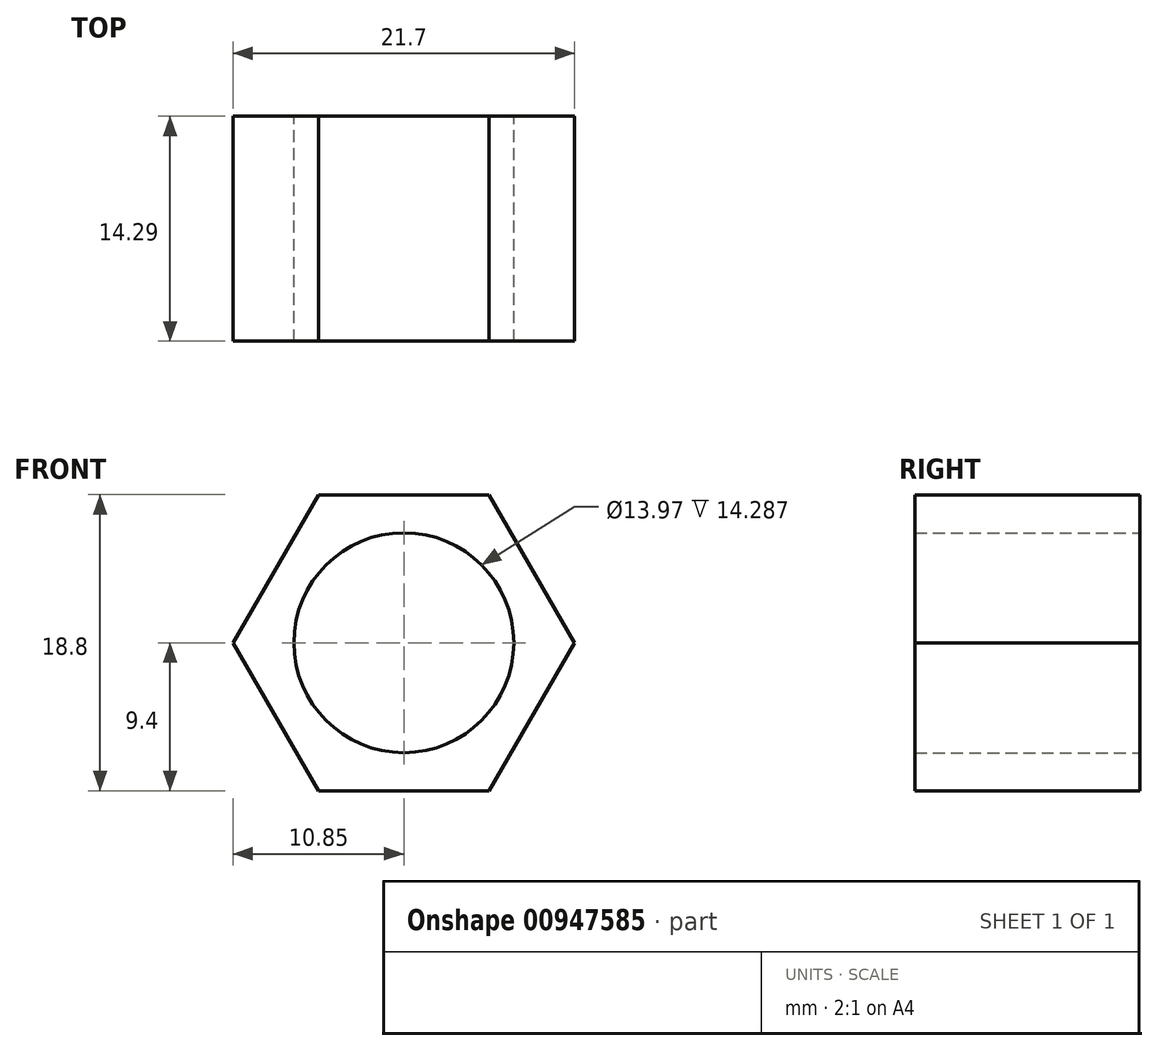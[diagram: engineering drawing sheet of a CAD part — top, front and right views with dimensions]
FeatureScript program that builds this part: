
annotation { "Feature Type Name" : "Feature", "Feature Type Description" : "" }
export const myFeature = defineFeature(function(context is Context, id is Id, definition is map)
    precondition{}
    {
        {
            var Q0;
            Q0=qCreatedBy(makeId("Front.planeOp"),FACE);
            var sketch = newSketch(context, id + "F0", { "sketchPlane" : qUnion([Q0])});
            skCircle(sketch, "E0.cCircle", {"center": v(0, 0) * mm, "radius": 9.4 * mm, "construction": true});
            skLineSegment(sketch, "E0.0", {"start": v(-5.43, 9.4) * mm, "end": v(5.43, 9.4) * mm});
            skLineSegment(sketch, "E0.1", {"start": v(5.43, 9.4) * mm, "end": v(10.85, 0) * mm});
            skLineSegment(sketch, "E0.2", {"start": v(10.85, 0) * mm, "end": v(5.43, -9.4) * mm});
            skLineSegment(sketch, "E0.3", {"start": v(5.43, -9.4) * mm, "end": v(-5.43, -9.4) * mm});
            skLineSegment(sketch, "E0.4", {"start": v(-5.43, -9.4) * mm, "end": v(-10.85, 0) * mm});
            skLineSegment(sketch, "E0.5", {"start": v(-10.85, 0) * mm, "end": v(-5.43, 9.4) * mm});
            skPoint(sketch, "E0.0.midPoint", {"position": v(0, 9.4) * mm});
            skCircle(sketch, "E1", {"center": v(0, 0) * mm, "radius": 6.99 * mm});
            skSolve(sketch);
        }
        {
            var Q0;
            Q0=makeQuery(id+"F0.imprint","IMPRINT",FACE,{"disambiguationData":[TD([[makeQuery(id+"F0.imprint","IMPRINT",EDGE,{"derivedFrom":sQuery(id+"F0.wireOp",EDGE,"E0.0")}),-1.0]])]});
            extrude(context, id + "F1", {"entities" : qUnion([Q0]), "depth" : 14.29 * mm, "offsetDistance" : 25.4 * mm});
        }
    });
